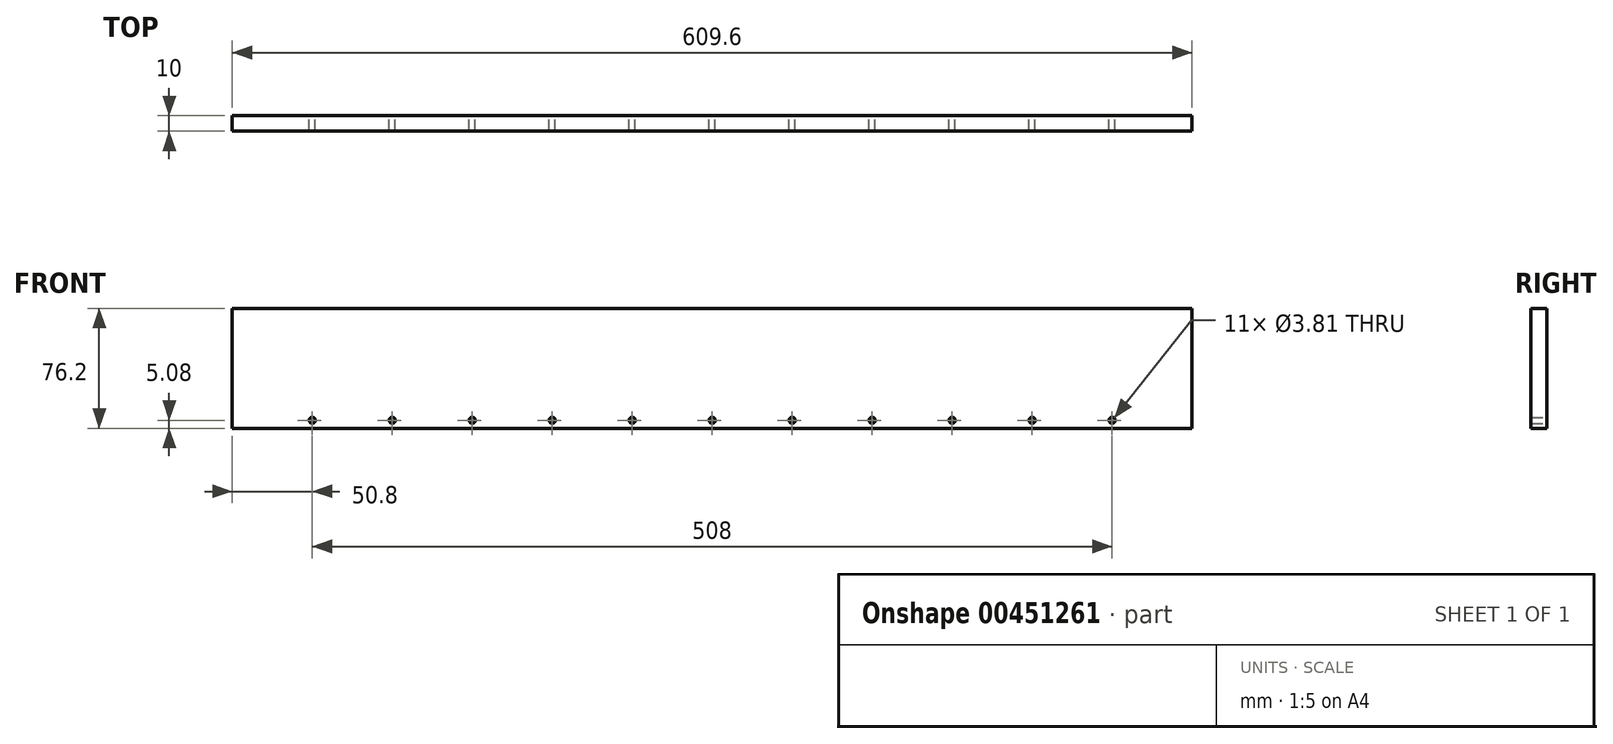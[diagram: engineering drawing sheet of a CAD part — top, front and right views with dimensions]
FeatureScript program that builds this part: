
annotation { "Feature Type Name" : "Feature", "Feature Type Description" : "" }
export const myFeature = defineFeature(function(context is Context, id is Id, definition is map)
    precondition{}
    {
        {
            var Q0;
            Q0=qCreatedBy(makeId("Front.planeOp"),FACE);
            var sketch = newSketch(context, id + "F0", { "sketchPlane" : qUnion([Q0])});
            skLineSegment(sketch, "E0.bottom", {"start": v(304.8, -38.1) * mm, "end": v(-304.8, -38.1) * mm});
            skLineSegment(sketch, "E0.top", {"start": v(304.8, 38.1) * mm, "end": v(-304.8, 38.1) * mm});
            skLineSegment(sketch, "E0.left", {"start": v(304.8, -38.1) * mm, "end": v(304.8, 38.1) * mm});
            skLineSegment(sketch, "E0.right", {"start": v(-304.8, -38.1) * mm, "end": v(-304.8, 38.1) * mm});
            skPoint(sketch, "E0.middle", {"position": v(0, 0) * mm});
            skCircle(sketch, "E1", {"center": v(-254, -33.02) * mm, "radius": 1.9 * mm});
            skCircle(sketch, "E2", {"center": v(-203.2, -33.02) * mm, "radius": 1.9 * mm});
            skCircle(sketch, "E3", {"center": v(-152.4, -33.02) * mm, "radius": 1.9 * mm});
            skCircle(sketch, "E4", {"center": v(-101.6, -33.02) * mm, "radius": 1.9 * mm});
            skCircle(sketch, "E5", {"center": v(-50.8, -33.02) * mm, "radius": 1.9 * mm});
            skCircle(sketch, "E6", {"center": v(0, -33.02) * mm, "radius": 1.9 * mm});
            skCircle(sketch, "E7", {"center": v(50.8, -33.02) * mm, "radius": 1.9 * mm});
            skCircle(sketch, "E8", {"center": v(101.6, -33.02) * mm, "radius": 1.9 * mm});
            skCircle(sketch, "E9", {"center": v(152.4, -33.02) * mm, "radius": 1.9 * mm});
            skCircle(sketch, "E10", {"center": v(203.2, -33.02) * mm, "radius": 1.9 * mm});
            skCircle(sketch, "E11", {"center": v(254, -33.02) * mm, "radius": 1.9 * mm});
            skLineSegment(sketch, "E12", {"start": v(-356.72, -33.02) * mm, "end": v(410.3, -33.02) * mm, "construction": true});
            skSolve(sketch);
        }
        {
            var Q0;
            Q0=makeQuery(id+"F0.imprint","IMPRINT",FACE,{"disambiguationData":[TD([[makeQuery(id+"F0.imprint","IMPRINT",EDGE,{"derivedFrom":sQuery(id+"F0.wireOp",EDGE,"E0.bottom")}),-1.0]])]});
            extrude(context, id + "F1", {"entities" : qUnion([Q0]), "depth" : 10 * mm});
        }
    });
